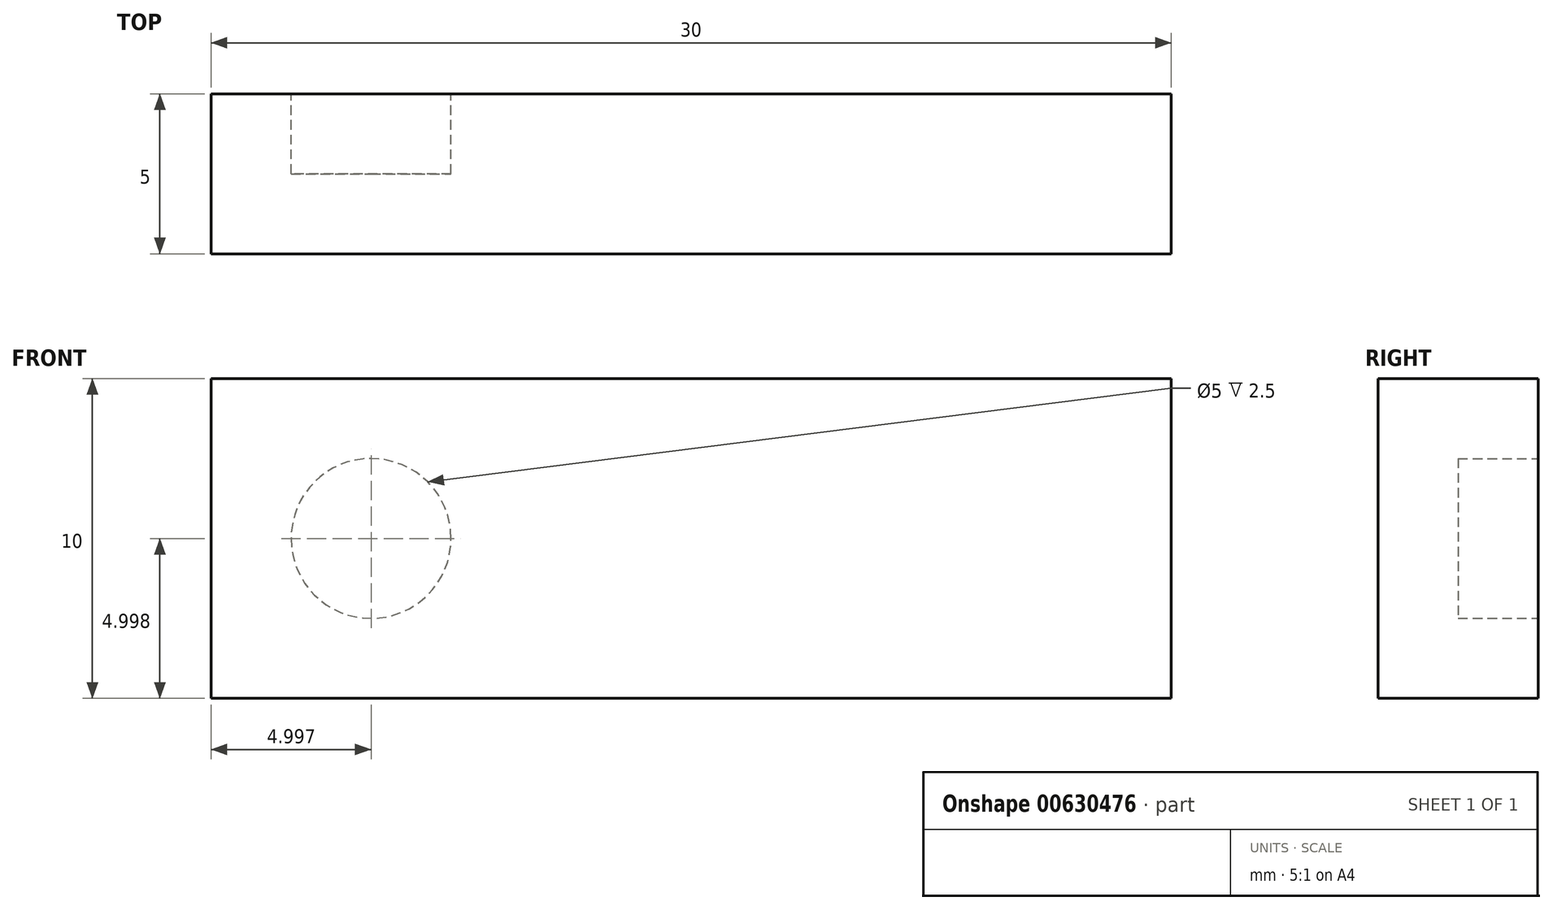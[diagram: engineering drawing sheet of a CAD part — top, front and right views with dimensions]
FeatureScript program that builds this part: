
annotation { "Feature Type Name" : "Feature", "Feature Type Description" : "" }
export const myFeature = defineFeature(function(context is Context, id is Id, definition is map)
    precondition{}
    {
        {
            var Q0;
            Q0=qCreatedBy(makeId("Front.planeOp"),FACE);
            var sketch = newSketch(context, id + "F0", { "sketchPlane" : qUnion([Q0])});
            skLineSegment(sketch, "E0.bottom", {"start": v(16.25, 24.26) * mm, "end": v(46.25, 24.26) * mm});
            skLineSegment(sketch, "E0.top", {"start": v(16.25, 14.26) * mm, "end": v(46.25, 14.26) * mm});
            skLineSegment(sketch, "E0.left", {"start": v(16.25, 24.26) * mm, "end": v(16.25, 14.26) * mm});
            skLineSegment(sketch, "E0.right", {"start": v(46.25, 24.26) * mm, "end": v(46.25, 14.26) * mm});
            skSolve(sketch);
        }
        {
            var Q0;
            Q0 = qSketchRegion(id + "F0", true);
            extrude(context, id + "F1", {"entities" : qUnion([Q0]), "depth" : 5 * mm, "offsetDistance" : 25 * mm});
        }
        {
            var Q0;
            Q0=makeQuery(id+"F1.opExtrude","CAP_FACE",FACE,{"disambiguationData":[OSD([sQuery(id+"F0.wireOp",EDGE,"E0.bottom"),sQuery(id+"F0.wireOp",EDGE,"E0.top"),sQuery(id+"F0.wireOp",EDGE,"E0.left"),sQuery(id+"F0.wireOp",EDGE,"E0.right")])],"isStart":true});
            var sketch = newSketch(context, id + "F2", { "sketchPlane" : qUnion([Q0])});
            skCircle(sketch, "E1", {"center": v(-21.25, 19.26) * mm, "radius": 2.5 * mm});
            skPoint(sketch, "E1.centerSnap0", {"position": v(-16.25, 19.26) * mm});
            skSolve(sketch);
        }
        {
            var Q0;
            Q0 = qSketchRegion(id + "F2", true);
            extrude(context, id + "F3", {"entities" : qUnion([Q0]), "operationType" : NewBodyOperationType.REMOVE, "oppositeDirection" : true, "depth" : 2.5 * mm, "offsetDistance" : 25 * mm});
        }
    });
